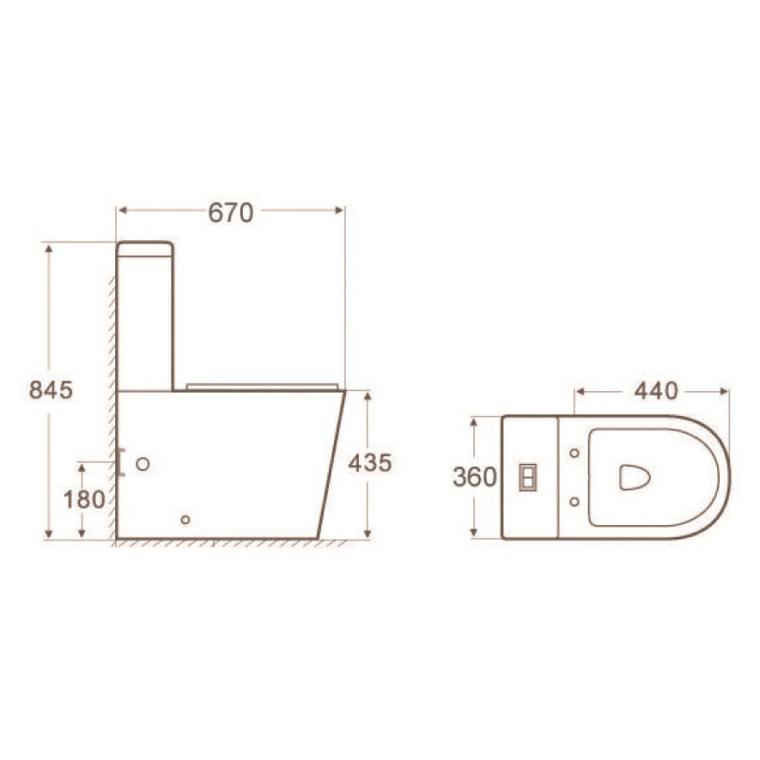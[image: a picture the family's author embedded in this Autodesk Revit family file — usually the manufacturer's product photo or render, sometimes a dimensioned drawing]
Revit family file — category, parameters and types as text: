
# Revit family: LIXIL - 431700WH - VAAL PARKTOWN FLOOR MOUNT PAN
name_source: partatom
category: Plumbing Fixtures
units: mm (PartAtom-declared; Revit-internal decimal feet)

## family parameters
Always vertical = Yes
Cut with Voids When Loaded = No
Enable Cutting in Views = No
Maintain Annotation Orientation = No
OmniClass Number = 23.45.00.00
OmniClass Title = Sanitary, Laundry, and Cleaning Equipment
Part Type = Normal
Room Calculation Point = No
Round Connector Dimension = Use Diameter
Shared = Yes
Work Plane-Based = No

## types (1)
- 431700WH
    Default Elevation = 0 mm  [stored 0 ft]
    Description = Vaal wc to detail and spec. See sanware schedule. Available from Lixil.
    Hosted on lixil.co.za = https://www.lixil.co.za
    M _ CISTERN = M _ LIXIL - VAAL - PORCELAIN - WHITE 01
    M _ WC = M _ LIXIL - VAAL - PORCELAIN - WHITE 01
    M _ WC LID AND SEAT = M _ LIXIL - VAAL - PLASTIC - WHITE 01
    M _ WC SEAT SS FITTINGS = M _ LIXIL - STAINLESS STEEL 01
    M _ WC SEAT SUPPORT = M _ LIXIL - VAAL - PLASTIC - WHITE 01
    Product Specification = Supplier: Lixil.
Product description: Vaal Parktown top-entry floor-mounted pan. Excludes seat. Suitable for commercial use. Compatible with the following Cobra exposed flush valves: FJ2-000/N, FJ2-001/N, FJ2-210/N, FM1-000/N, FM1-210/N, FM1-214/N, FM2-210/N & FM2-214/N. Dimensions: 550mm long, 360mm wide, 420mm high. 10 Year LIXIL Africa warranty. Access to Cobra TeamAssist technical team.
10 Year Warranty Cobra TeamAssist.
Product Code: 1046380200.
SKU Code	: 431700WH.
Barcode: 6005826072891.
Brand: Vaal.
Range: Parktown.
Category: Toilets.
Sub-Category: Pans.
Material: Ceramic.
Colour: White.
Package Height: 420 mm
Package Width: 360 mm
Package Length: 550 mm
Product Height: 420mm
Product Width: 360 mm
Product Length: 550 mm
Package Volume: 83160000 mm³
Package Weight: 45.24 kg

Notes:
- Refer to manufacturer's and supplier's installation, maintenance and cleaning manual.
- Refer to manufacturer's and supplier's guarantees and warrantees document.

note: [stored X ft] marks values corroborated as IEEE doubles in the binary element streams (Revit-internal decimal feet)

## geometry (parser evidence)
native form markers: Sweep x21
no freeform markers — native parametric forms only
